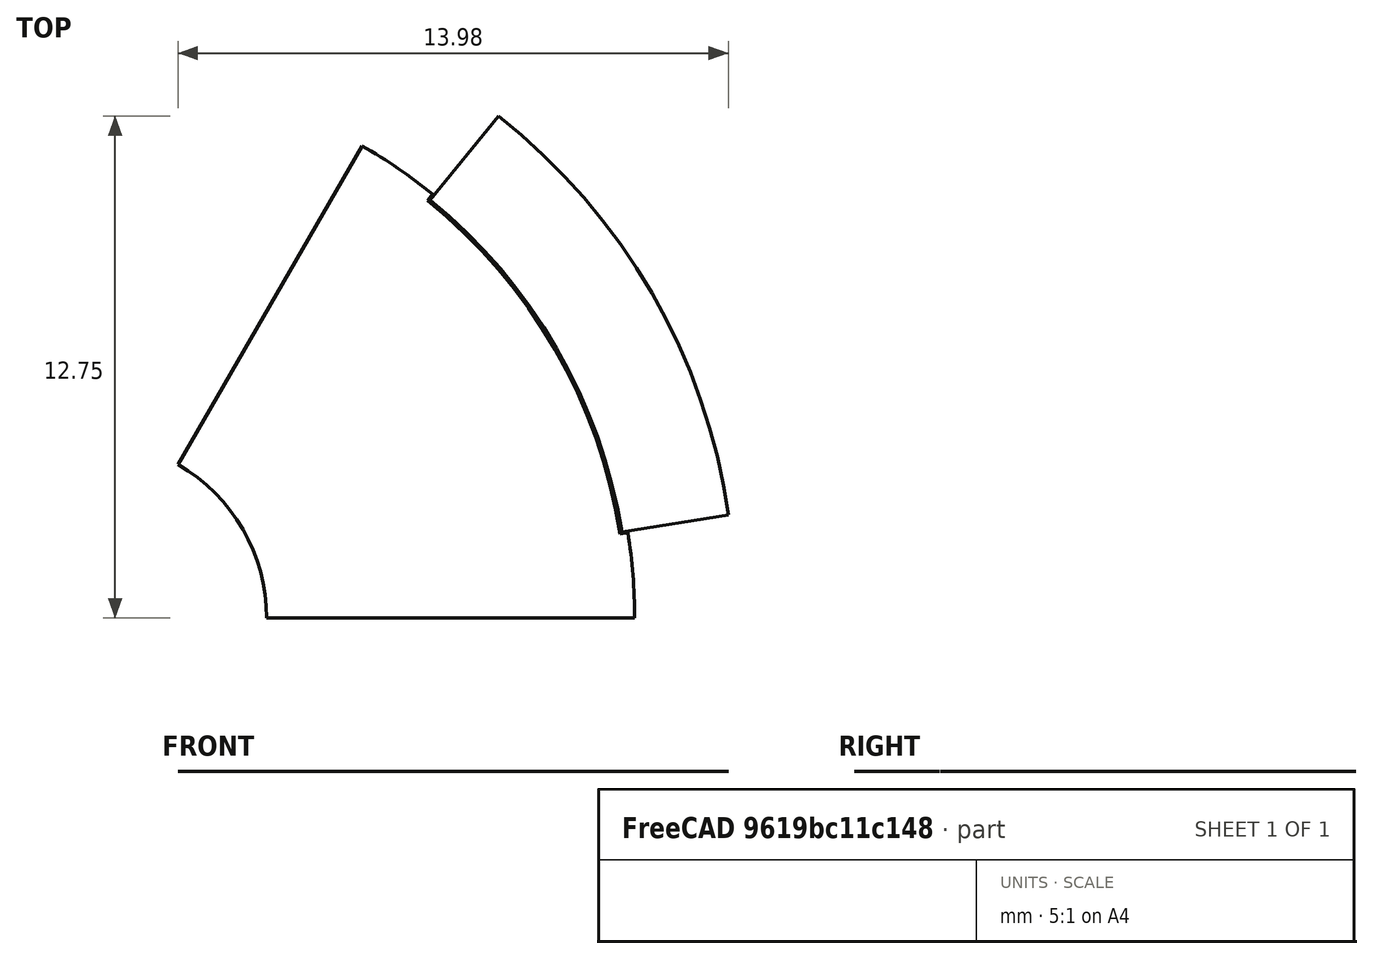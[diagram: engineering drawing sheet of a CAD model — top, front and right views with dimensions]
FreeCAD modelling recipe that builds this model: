
FCSTD DOCUMENT  (FreeCAD 0.18R4 (GitTag))
Label: rotor3
License: All rights reserved
LicenseURL: http://en.wikipedia.org/wiki/All_rights_reserved
objects: Sketcher::SketchObject×5, PartDesign::Body×2, Surface::Filling×2, Spreadsheet::Sheet×1
note: 9 computed .brp shape members not serialized (recipe doc carries the construction recipe); baked Part::Feature solids carry a one-line shape summary decoded from their .brp

FEATURE [Spreadsheet::Sheet] Spreadsheet  label="Variables"
  cells = A2=poleNumber; B2(poleNumber)=6; A3=outerDiameter; B3(outerDiameter)=33; D3=Calc Value; A4=innerDiameter; B4(innerDiameter)=9; D4=Input Value; A5=stackLength; B5(stackLength)=20; A6=stackingFactor; B6(stackingFactor)=0.95; A7=embrace; B7(embrace)=75; A8=contourRatio; B8(contourRatio)=90; A9=magnetAirgap; B9(magnetAirgap)=0.05; A10=poleSeparation; B10(poleSeparation)=2; A11=magnetWidth; B11(magnetWidth)=9; A12=magnetHeight; B12(magnetHeight)=2.8; A13=rib; B13(rib)=0.5; A14=bridgeCurved; B14(bridgeCurved)=0.5; A15=cutTop; B15(cutTop)=0.2; A16=cutBottom; B16(cutBottom)=0.25; A17=segmentAngle; B17(segmentAngle)==360 / poleNumber; A18=movePocketInwards; B18(movePocketInwards)=0.5; A19=cuttingThickness; B19(cuttingThickness)=0.1; A20=magnetLength; B20(magnetLength)==stackLength; A21=cut; B21(cut)=0.2; A22=ribShaft; B22(ribShaft)=0.5; A23=magnetEmbrace; B23(magnetEmbrace)=70; A24=magnetContourRatio; B24(magnetContourRatio)=95; A25=axialMisalignment; B25(axialMisalignment)=0.5
FEATURE [Sketcher::SketchObject] Sketch003  label="RotorSketch"
  MapMode = 5
  Support = -> [XY_Plane]
  expr: Constraints[37] = Variables.outerDiameter / 2 - Variables.magnetHeight - Variables.magnetAirgap
  expr: Constraints[32] = Variables.outerDiameter / 2 - Variables.magnetHeight - Variables.magnetAirgap + Spreadsheet.cut
  expr: Constraints[28] = Variables.segmentAngle * Variables.magnetEmbrace / 100
  expr: Constraints[15] = Variables.outerDiameter / 2
  expr: Constraints[14] = Variables.innerDiameter / 2
  expr: Constraints[18] = Variables.segmentAngle / 2
  expr: Constraints[0] = Variables.segmentAngle
  expr: Constraints[23] = Variables.outerDiameter / 2 * Variables.magnetContourRatio / 100
  sketch-geometry (20):
    g0: LineSegment [constr] StartX=4.5 StartY=0 StartZ=0 EndX=16.5 EndY=0 EndZ=0
    g1: LineSegment [constr] StartX=2.25 StartY=3.89711 StartZ=0 EndX=8.25 EndY=14.2894 EndZ=0
    g2: LineSegment [constr] StartX=0 StartY=0 StartZ=0 EndX=4.5 EndY=0 EndZ=0
    g3: LineSegment [constr] StartX=0 StartY=0 StartZ=0 EndX=2.25 EndY=3.89711 EndZ=0
    g4: ArcOfCircle [constr] CenterX=0 CenterY=0 CenterZ=0 NormalX=0 NormalY=0 NormalZ=1 AngleXU=0 Radius=16.5 StartAngle=0 EndAngle=1.0472
    g5: ArcOfCircle CenterX=0 CenterY=0 CenterZ=0 NormalX=0 NormalY=0 NormalZ=1 AngleXU=0 Radius=4.5 StartAngle=0 EndAngle=1.0472
    g6: LineSegment [constr] StartX=0 StartY=0 StartZ=0 EndX=14.2894 EndY=8.25 EndZ=0
    g7: ArcOfCircle [constr] CenterX=0.714471 CenterY=0.4125 CenterZ=0 NormalX=0 NormalY=0 NormalZ=1 AngleXU=0 Radius=15.675 StartAngle=6.25687 EndAngle=7.3567
    g8: LineSegment [constr] StartX=0 StartY=0 StartZ=0 EndX=10.3838 EndY=12.8229 EndZ=0
    g9: LineSegment [constr] StartX=0 StartY=0 StartZ=0 EndX=16.2969 EndY=2.58117 EndZ=0
    g10: ArcOfCircle [constr] CenterX=0 CenterY=0 CenterZ=0 NormalX=0 NormalY=0 NormalZ=1 AngleXU=0 Radius=13.85 StartAngle=0 EndAngle=1.0472
    g11: LineSegment [constr] StartX=0 StartY=0 StartZ=0 EndX=8.59022 EndY=10.608 EndZ=0
    g12: LineSegment [constr] StartX=0 StartY=0 StartZ=0 EndX=13.4819 EndY=2.13533 EndZ=0
    g13: ArcOfCircle CenterX=0 CenterY=0 CenterZ=0 NormalX=0 NormalY=0 NormalZ=1 AngleXU=0 Radius=13.65 StartAngle=0.15708 EndAngle=0.890118
    g14: ArcOfCircle CenterX=0 CenterY=0 CenterZ=0 NormalX=0 NormalY=0 NormalZ=1 AngleXU=0 Radius=13.85 StartAngle=0.890118 EndAngle=1.0472
    g15: ArcOfCircle CenterX=0 CenterY=0 CenterZ=0 NormalX=0 NormalY=0 NormalZ=1 AngleXU=0 Radius=13.85 StartAngle=0 EndAngle=0.15708
    g16: LineSegment StartX=8.71609 StartY=10.7635 StartZ=0 EndX=8.59022 EndY=10.608 EndZ=0
    g17: LineSegment StartX=13.4819 StartY=2.13533 StartZ=0 EndX=13.6795 EndY=2.16662 EndZ=0
    g18: LineSegment StartX=2.25 StartY=3.89711 StartZ=0 EndX=6.925 EndY=11.9945 EndZ=0
    g19: LineSegment StartX=4.5 StartY=0 StartZ=0 EndX=13.85 EndY=0 EndZ=0
  constraints (56):
    c: Angle(g0,g1) = 1.0472
    c: Coincident(g2,g-1)
    c: Coincident(g2,g0)
    c: Coincident(g3,g2)
    c: Coincident(g3,g1)
    c: Parallel(g2,g0)
    c: Parallel(g3,g1)
    c: Coincident(g4,g-1)
    c: Coincident(g4,g0)
    c: Coincident(g4,g1)
    c: Coincident(g5,g4)
    c: Coincident(g5,g1)
    c: Coincident(g5,g0)
    c: Angle(g-1,g2) = 0
    c: Radius(g5) = 4.5
    c: Radius(g4) = 16.5
    c: Coincident(g6,g5)
    c: PointOnObject(g6,g4)
    c: Angle(g-1,g6) = 0.523599
    c: PointOnObject(g7,g1)
    c: PointOnObject(g7,g0)
    c: PointOnObject(g6,g7)
    c: PointOnObject(g7,g6)
    c: Radius(g7) = 15.675
    c: Coincident(g8,g5)
    c: PointOnObject(g8,g4)
    c: Coincident(g9,g5)
    c: Symmetric(g8,g9,g6)
    c: Angle(g9,g8) = 0.733038
    c: Coincident(g10,g5)
    c: PointOnObject(g10,g1)
    c: PointOnObject(g10,g0)
    c: Radius(g10) = 13.85
    c: Coincident(g11,g5)
    c: PointOnObject(g11,g8)
    c: Coincident(g12,g5)
    c: PointOnObject(g12,g9)
    c: Distance(g12) = 13.65
    c: Coincident(g13,g5)
    c: Coincident(g13,g11)
    c: PointOnObject(g13,g9)
    c: Coincident(g14,g5)
    c: Coincident(g14,g10)
    c: PointOnObject(g14,g8)
    c: Coincident(g15,g5)
    c: Coincident(g15,g10)
    c: PointOnObject(g15,g9)
    c: Coincident(g16,g14)
    c: Coincident(g16,g13)
    c: Coincident(g17,g13)
    c: Coincident(g17,g15)
    c: Coincident(g18,g5)
    c: Coincident(g18,g14)
    c: Coincident(g19,g5)
    c: Coincident(g19,g15)
    c: Equal(g11,g12)
FEATURE [Sketcher::SketchObject] Sketch004  label="BoundingBox"
  MapMode = 5
  Support = -> [XY_Plane]
  expr: Constraints[8] = Variables.outerDiameter
  sketch-geometry (6):
    g0: LineSegment StartX=-16.5 StartY=-16.5 StartZ=0 EndX=16.5 EndY=-16.5 EndZ=0
    g1: LineSegment StartX=16.5 StartY=-16.5 StartZ=0 EndX=16.5 EndY=16.5 EndZ=0
    g2: LineSegment StartX=16.5 StartY=16.5 StartZ=0 EndX=-16.5 EndY=16.5 EndZ=0
    g3: LineSegment StartX=-16.5 StartY=16.5 StartZ=0 EndX=-16.5 EndY=-16.5 EndZ=0
    g4: LineSegment [constr] StartX=-16.5 StartY=-16.5 StartZ=0 EndX=16.5 EndY=16.5 EndZ=0
    g5: GeomPoint X=0 Y=0 Z=0
  constraints (14):
    c: Coincident(g0,g1)
    c: Coincident(g1,g2)
    c: Coincident(g2,g3)
    c: Coincident(g3,g0)
    c: Horizontal(g0)
    c: Horizontal(g2)
    c: Vertical(g1)
    c: Vertical(g3)
    c: DistanceY(g1,g1) = 33
    c: Equal(g2,g1)
    c: Coincident(g4,g0)
    c: Coincident(g4,g1)
    c: Symmetric(g0,g1,g5)
    c: Coincident(g-1,g5)
FEATURE [Sketcher::SketchObject] Sketch005  label="RotorSideSketch"
  MapMode = 5
  Support = -> [XY_Plane001]
  expr: Constraints[22] = Variables.stackLength / 2 - Variables.axialMisalignment
  expr: Constraints[9] = Variables.outerDiameter / 2
  expr: Constraints[8] = Variables.innerDiameter / 2
  expr: Constraints[7] = Variables.stackLength
  sketch-geometry (8):
    g0: LineSegment StartX=-9.5 StartY=4.5 StartZ=0 EndX=10.5 EndY=4.5 EndZ=0
    g1: LineSegment StartX=10.5 StartY=4.5 StartZ=0 EndX=10.5 EndY=16.5 EndZ=0
    g2: LineSegment StartX=10.5 StartY=16.5 StartZ=0 EndX=-9.5 EndY=16.5 EndZ=0
    g3: LineSegment StartX=-9.5 StartY=16.5 StartZ=0 EndX=-9.5 EndY=4.5 EndZ=0
    g4: LineSegment StartX=-9.5 StartY=-4.5 StartZ=0 EndX=10.5 EndY=-4.5 EndZ=0
    g5: LineSegment StartX=10.5 StartY=-4.5 StartZ=0 EndX=10.5 EndY=-16.5 EndZ=0
    g6: LineSegment StartX=10.5 StartY=-16.5 StartZ=0 EndX=-9.5 EndY=-16.5 EndZ=0
    g7: LineSegment StartX=-9.5 StartY=-16.5 StartZ=0 EndX=-9.5 EndY=-4.5 EndZ=0
  constraints (23):
    c: Coincident(g0,g1)
    c: Coincident(g1,g2)
    c: Coincident(g2,g3)
    c: Coincident(g3,g0)
    c: Horizontal(g0)
    c: Vertical(g1)
    c: Vertical(g3)
    c: DistanceX(g2,g2) = 20
    c: DistanceY(g-1,g0) = 4.5
    c: DistanceY(g-1,g1) = 16.5
    c: Coincident(g4,g5)
    c: Coincident(g5,g6)
    c: Coincident(g6,g7)
    c: Coincident(g7,g4)
    c: Horizontal(g4)
    c: Vertical(g5)
    c: Vertical(g7)
    c: Equal(g4,g0)
    c: Equal(g7,g3)
    c: Horizontal(g6)
    c: Horizontal(g2)
    c: Symmetric(g4,g0,g-1)
    c: DistanceX(g0,g-1) = 9.5
FEATURE [Sketcher::SketchObject] Sketch006  label="MagnetSideSketch"
  ExternalGeometry = -> [Sketch005]
  MapMode = 5
  Support = -> [XY_Plane001]
  expr: Constraints[20] = Variables.stackLength / 2 - Variables.axialMisalignment
  expr: Constraints[7] = Variables.magnetHeight
  sketch-geometry (8):
    g0: LineSegment StartX=-9.5 StartY=13.7 StartZ=0 EndX=10.5 EndY=13.7 EndZ=0
    g1: LineSegment StartX=10.5 StartY=13.7 StartZ=0 EndX=10.5 EndY=16.5 EndZ=0
    g2: LineSegment StartX=10.5 StartY=16.5 StartZ=0 EndX=-9.5 EndY=16.5 EndZ=0
    g3: LineSegment StartX=-9.5 StartY=16.5 StartZ=0 EndX=-9.5 EndY=13.7 EndZ=0
    g4: LineSegment StartX=-9.5 StartY=-16.5 StartZ=0 EndX=10.5 EndY=-16.5 EndZ=0
    g5: LineSegment StartX=10.5 StartY=-16.5 StartZ=0 EndX=10.5 EndY=-13.7 EndZ=0
    g6: LineSegment StartX=10.5 StartY=-13.7 StartZ=0 EndX=-9.5 EndY=-13.7 EndZ=0
    g7: LineSegment StartX=-9.5 StartY=-13.7 StartZ=0 EndX=-9.5 EndY=-16.5 EndZ=0
  constraints (21):
    c: Coincident(g0,g1)
    c: Coincident(g1,g2)
    c: Coincident(g2,g3)
    c: Coincident(g3,g0)
    c: Horizontal(g0)
    c: Vertical(g1)
    c: Vertical(g3)
    c: DistanceY(g1,g1) = 2.8
    c: Coincident(g4,g5)
    c: Coincident(g5,g6)
    c: Coincident(g6,g7)
    c: Coincident(g7,g4)
    c: Horizontal(g4)
    c: Vertical(g5)
    c: Vertical(g7)
    c: Symmetric(g6,g0,g-1)
    c: Symmetric(g5,g0,g-1)
    c: Equal(g7,g3)
    c: Coincident(g1,g-3)
    c: Horizontal(g2)
    c: DistanceX(g0,g-1) = 9.5
FEATURE [PartDesign::Body] Body001  label="SideView"
  Group = -> [Sketch005,Sketch006]
  Origin = -> Origin001
FEATURE [Sketcher::SketchObject] Sketch007  label="MagnetSketch"
  MapMode = 5
  Support = -> [XY_Plane]
  expr: Constraints[35] = Variables.outerDiameter / 2 - Variables.magnetHeight - Variables.magnetAirgap
  expr: Constraints[18] = Variables.segmentAngle / 2
  expr: Constraints[0] = Variables.segmentAngle
  expr: Constraints[30] = Variables.outerDiameter / 2 - Variables.magnetHeight - Variables.magnetAirgap + Spreadsheet.cut
  expr: Constraints[21] = Variables.outerDiameter / 2 * Variables.magnetContourRatio / 100
  expr: Constraints[26] = Variables.segmentAngle * Variables.magnetEmbrace / 100
  expr: Constraints[69] = Variables.outerDiameter / 2 - Variables.magnetHeight
  expr: Constraints[15] = Variables.outerDiameter / 2
  expr: Constraints[14] = Variables.innerDiameter / 2
  expr: Constraints[59] = Variables.magnetAirgap
  sketch-geometry (27):
    g0: LineSegment [constr] StartX=4.5 StartY=0 StartZ=0 EndX=16.5 EndY=0 EndZ=0
    g1: LineSegment [constr] StartX=2.25 StartY=3.89711 StartZ=0 EndX=8.25 EndY=14.2894 EndZ=0
    g2: LineSegment [constr] StartX=0 StartY=0 StartZ=0 EndX=4.5 EndY=0 EndZ=0
    g3: LineSegment [constr] StartX=0 StartY=0 StartZ=0 EndX=2.25 EndY=3.89711 EndZ=0
    g4: ArcOfCircle [constr] CenterX=0 CenterY=0 CenterZ=0 NormalX=0 NormalY=0 NormalZ=1 AngleXU=0 Radius=16.5 StartAngle=0 EndAngle=1.0472
    g5: ArcOfCircle [constr] CenterX=0 CenterY=0 CenterZ=0 NormalX=0 NormalY=0 NormalZ=1 AngleXU=0 Radius=4.5 StartAngle=0 EndAngle=1.0472
    g6: LineSegment [constr] StartX=0 StartY=0 StartZ=0 EndX=14.2894 EndY=8.25 EndZ=0
    g7: ArcOfCircle CenterX=0.714471 CenterY=0.4125 CenterZ=0 NormalX=0 NormalY=0 NormalZ=1 AngleXU=0 Radius=15.675 StartAngle=0.141402 EndAngle=0.905796
    g8: LineSegment [constr] StartX=0 StartY=0 StartZ=0 EndX=10.3838 EndY=12.8229 EndZ=0
    g9: LineSegment [constr] StartX=0 StartY=0 StartZ=0 EndX=16.2969 EndY=2.58117 EndZ=0
    g10: ArcOfCircle [constr] CenterX=0 CenterY=0 CenterZ=0 NormalX=0 NormalY=0 NormalZ=1 AngleXU=0 Radius=13.85 StartAngle=0 EndAngle=1.0472
    g11: LineSegment [constr] StartX=0 StartY=0 StartZ=0 EndX=8.59022 EndY=10.608 EndZ=0
    g12: LineSegment [constr] StartX=0 StartY=0 StartZ=0 EndX=13.4819 EndY=2.13533 EndZ=0
    g13: ArcOfCircle [constr] CenterX=0 CenterY=0 CenterZ=0 NormalX=0 NormalY=0 NormalZ=1 AngleXU=0 Radius=13.65 StartAngle=0.15708 EndAngle=0.890118
    g14: ArcOfCircle [constr] CenterX=0 CenterY=0 CenterZ=0 NormalX=0 NormalY=0 NormalZ=1 AngleXU=0 Radius=13.85 StartAngle=0.890118 EndAngle=1.0472
    g15: ArcOfCircle [constr] CenterX=0 CenterY=0 CenterZ=0 NormalX=0 NormalY=0 NormalZ=1 AngleXU=0 Radius=13.85 StartAngle=0 EndAngle=0.15708
    g16: LineSegment [constr] StartX=8.71609 StartY=10.7635 StartZ=0 EndX=8.59022 EndY=10.608 EndZ=0
    g17: LineSegment [constr] StartX=13.4819 StartY=2.13533 StartZ=0 EndX=13.6795 EndY=2.16662 EndZ=0
    g18: LineSegment [constr] StartX=2.25 StartY=3.89711 StartZ=0 EndX=6.925 EndY=11.9945 EndZ=0
    g19: LineSegment [constr] StartX=4.5 StartY=0 StartZ=0 EndX=13.85 EndY=0 EndZ=0
    g20: LineSegment [constr] StartX=8.62568 StartY=10.5792 StartZ=0 EndX=10.4226 EndY=12.7914 EndZ=0
    g21: LineSegment [constr] StartX=10.4226 StartY=12.7914 StartZ=0 EndX=10.3838 EndY=12.8229 EndZ=0
    g22: LineSegment [constr] StartX=13.6722 StartY=2.21202 StartZ=0 EndX=16.289 EndY=2.63054 EndZ=0
    g23: LineSegment [constr] StartX=16.289 StartY=2.63054 StartZ=0 EndX=16.2969 EndY=2.58117 EndZ=0
    g24: ArcOfCircle CenterX=0 CenterY=0 CenterZ=0 NormalX=0 NormalY=0 NormalZ=1 AngleXU=0 Radius=13.7 StartAngle=0.16042 EndAngle=0.886778
    g25: LineSegment StartX=8.6572 StartY=10.618 StartZ=0 EndX=10.3869 EndY=12.7474 EndZ=0
    g26: LineSegment StartX=13.5241 StartY=2.18833 StartZ=0 EndX=16.233 EndY=2.62159 EndZ=0
  constraints (76):
    c: Angle(g0,g1) = 1.0472
    c: Coincident(g2,g-1)
    c: Coincident(g2,g0)
    c: Coincident(g3,g2)
    c: Coincident(g3,g1)
    c: Parallel(g2,g0)
    c: Parallel(g3,g1)
    c: Coincident(g4,g-1)
    c: Coincident(g4,g0)
    c: Coincident(g4,g1)
    c: Coincident(g5,g4)
    c: Coincident(g5,g1)
    c: Coincident(g5,g0)
    c: Angle(g-1,g2) = 0
    c: Radius(g5) = 4.5
    c: Radius(g4) = 16.5
    c: Coincident(g6,g5)
    c: PointOnObject(g6,g4)
    c: Angle(g-1,g6) = 0.523599
    c: PointOnObject(g6,g7)
    c: PointOnObject(g7,g6)
    c: Radius(g7) = 15.675
    c: Coincident(g8,g5)
    c: PointOnObject(g8,g4)
    c: Coincident(g9,g5)
    c: Symmetric(g8,g9,g6)
    c: Angle(g9,g8) = 0.733038
    c: Coincident(g10,g5)
    c: PointOnObject(g10,g1)
    c: PointOnObject(g10,g0)
    c: Radius(g10) = 13.85
    c: Coincident(g11,g5)
    c: PointOnObject(g11,g8)
    c: Coincident(g12,g5)
    c: PointOnObject(g12,g9)
    c: Distance(g12) = 13.65
    c: Coincident(g13,g5)
    c: Coincident(g13,g11)
    c: PointOnObject(g13,g9)
    c: Coincident(g14,g5)
    c: Coincident(g14,g10)
    c: PointOnObject(g14,g8)
    c: Coincident(g15,g5)
    c: Coincident(g15,g10)
    c: PointOnObject(g15,g9)
    c: Coincident(g16,g14)
    c: Coincident(g16,g13)
    c: Coincident(g17,g13)
    c: Coincident(g17,g15)
    c: Coincident(g18,g5)
    c: Coincident(g18,g14)
    c: Coincident(g19,g5)
    c: Coincident(g19,g15)
    c: Equal(g11,g12)
    c: PointOnObject(g20,g13)
    c: PointOnObject(g20,g4)
    c: Coincident(g21,g20)
    c: Coincident(g21,g8)
    c: Angle(g21,g20) = 1.5708
    c: Distance(g21) = 0.05
    c: PointOnObject(g22,g10)
    c: PointOnObject(g22,g4)
    c: Coincident(g23,g22)
    c: Coincident(g23,g9)
    c: Angle(g22,g23) = 1.5708
    c: Equal(g23,g21)
    c: Coincident(g24,g5)
    c: PointOnObject(g24,g22)
    c: PointOnObject(g24,g20)
    c: Radius(g24) = 13.7
    c: PointOnObject(g7,g20)
    c: PointOnObject(g7,g22)
    c: Coincident(g25,g24)
    c: Coincident(g25,g7)
    c: Coincident(g26,g24)
    c: Coincident(g26,g7)
FEATURE [PartDesign::Body] Body  label="TopView"
  Group = -> [Sketch003,Sketch004,Sketch007]
  Origin = -> Origin
FEATURE [Surface::Filling] Surface  label="Rotor_Surface"
  Anisotropy = false
  BoundaryEdges = -> [Sketch003]
  BoundaryOrder = [0,0,0,0,0,0,0,0]
  Degree = 3
  Iterations = 2
  MaximumDegree = 8
  MaximumSegments = 9
  PointsOnCurve = 15
  TolAngular = 0.01
  TolCurvature = 0.1
  Tolerance2d = 1e-05
  Tolerance3d = 0.0001
FEATURE [Surface::Filling] Surface001  label="Magnet_Surface"
  Anisotropy = false
  BoundaryEdges = -> [Sketch007]
  BoundaryOrder = [0,0,0,0]
  Degree = 3
  Iterations = 2
  MaximumDegree = 8
  MaximumSegments = 9
  PointsOnCurve = 15
  TolAngular = 0.01
  TolCurvature = 0.1
  Tolerance2d = 1e-05
  Tolerance3d = 0.0001
